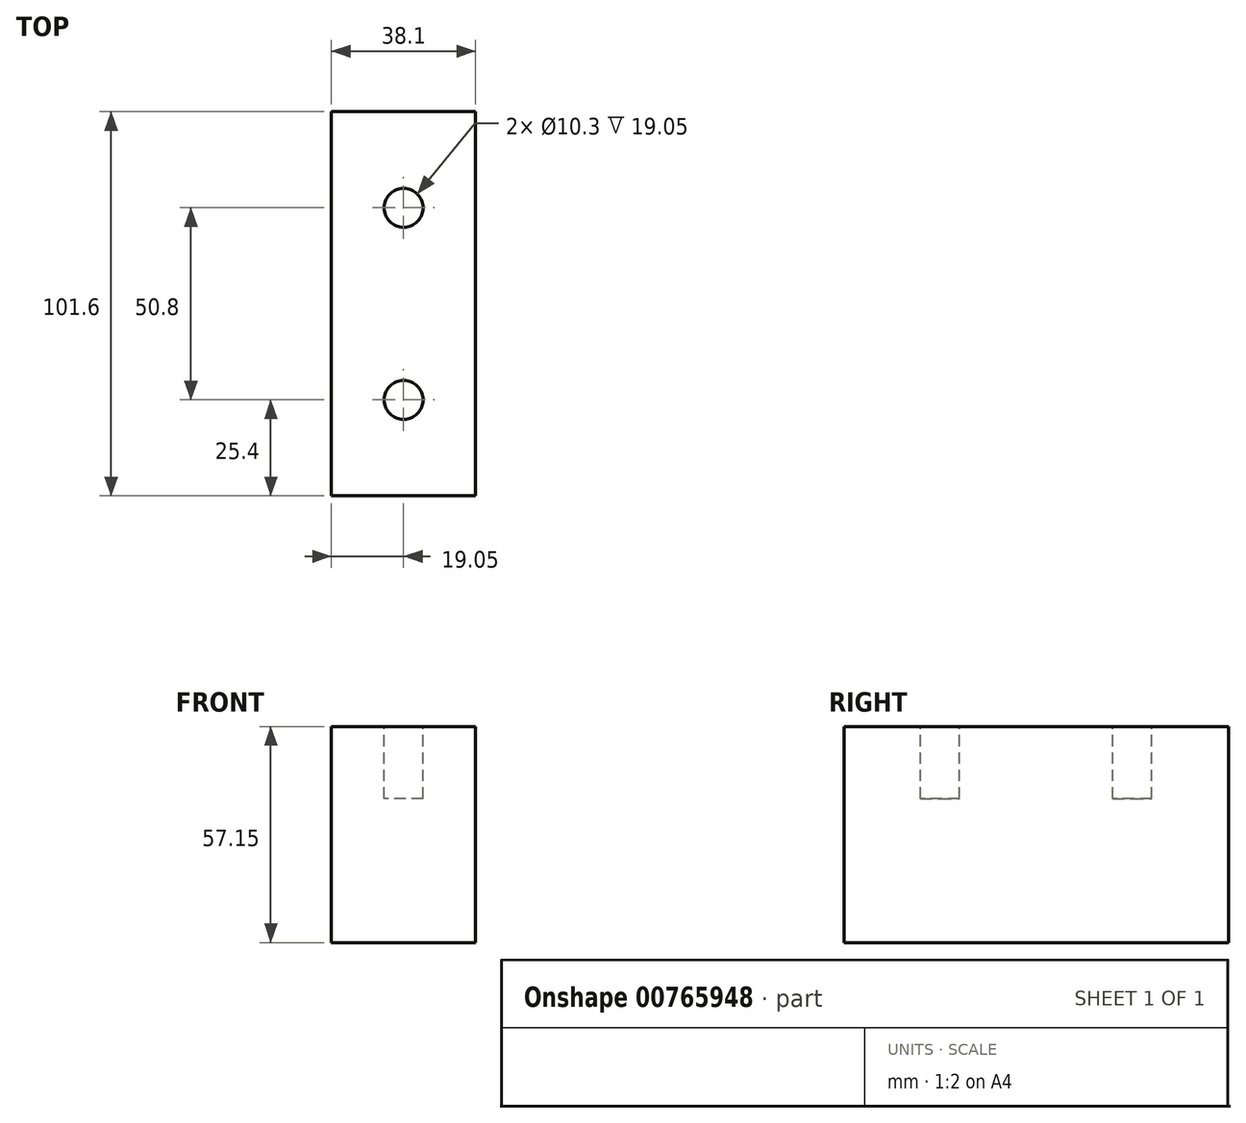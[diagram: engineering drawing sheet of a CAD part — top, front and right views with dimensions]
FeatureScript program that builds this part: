
annotation { "Feature Type Name" : "Feature", "Feature Type Description" : "" }
export const myFeature = defineFeature(function(context is Context, id is Id, definition is map)
    precondition{}
    {
        {
            var Q0;
            Q0=qCreatedBy(makeId("Front.planeOp"),FACE);
            var sketch = newSketch(context, id + "F0", { "sketchPlane" : qUnion([Q0])});
            skLineSegment(sketch, "E0.bottom", {"start": v(0, 0) * mm, "end": v(38.1, 0) * mm});
            skLineSegment(sketch, "E0.top", {"start": v(0, 57.15) * mm, "end": v(38.1, 57.15) * mm});
            skLineSegment(sketch, "E0.left", {"start": v(0, 0) * mm, "end": v(0, 57.15) * mm});
            skLineSegment(sketch, "E0.right", {"start": v(38.1, 0) * mm, "end": v(38.1, 57.15) * mm});
            skSolve(sketch);
        }
        {
            var Q0;
            Q0 = qSketchRegion(id + "F0", true);
            extrude(context, id + "F1", {"entities" : qUnion([Q0]), "depth" : 101.6 * mm, "offsetDistance" : 25.4 * mm});
        }
        {
            var Q0;
            Q0=makeQuery(id+"F1.opExtrude","SWEPT_FACE",FACE,{"disambiguationData":[OSD([sQuery(id+"F0.wireOp",EDGE,"E0.top")])]});
            var sketch = newSketch(context, id + "F2", { "sketchPlane" : qUnion([Q0])});
            skLineSegment(sketch, "E1", {"start": v(19.05, 0) * mm, "end": v(19.05, -101.6) * mm, "construction": true});
            skCircle(sketch, "E2", {"center": v(19.05, -25.4) * mm, "radius": 5.15 * mm});
            skCircle(sketch, "E3", {"center": v(19.05, -76.2) * mm, "radius": 5.15 * mm});
            skSolve(sketch);
        }
        {
            var Q0;
            Q0 = qSketchRegion(id + "F2", true);
            extrude(context, id + "F3", {"entities" : qUnion([Q0]), "operationType" : NewBodyOperationType.REMOVE, "oppositeDirection" : true, "depth" : 19.05 * mm, "offsetDistance" : 25.4 * mm});
        }
    });
